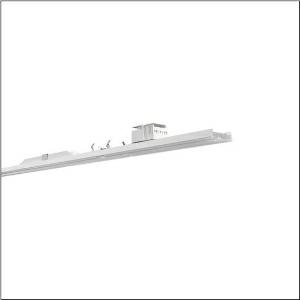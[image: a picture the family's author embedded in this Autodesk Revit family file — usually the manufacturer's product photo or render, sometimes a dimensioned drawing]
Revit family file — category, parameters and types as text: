
# Revit family: licross_r__11_recessed_mo_51tl11dv4fxf_3342
name_source: partatom
category: Lighting Fixtures
units: mm (PartAtom-declared; Revit-internal decimal feet)

## family parameters
Cut with Voids When Loaded = No
Host = Face
Light Source = No
Part Type = Normal
Room Calculation Point = No
Round Connector Dimension = Use Diameter
Shared = No

## types (1)
- --- (1 x LED, 15190 lm, 89.6 W, 4000K)
    Apparent Load = 90 VA
    CIE Flux Codes = 89 96 99 100 100
    Color Rendering = 80
    Color Temperature = 4000K
    Default Elevation = 1800 mm
    Description = Licross® 11 Recessed MOluminaire insert, length: 2.250mm, width: 66mm, height: 67mm, LED rated luminous flux: 15.190lm, light colour: 840, control gear: DALI 2, control gear: ECG DALI, with plug, 5-pole, with phase selection, mains connection: 220..240V, AC, 50/60Hz, halogen-free wiring, primary optical cover: cover, of PMMA, light emission: direct distribution, protection rating (complete): IP40, insulation class (complete): insulation class I (protective earthing), certification: CE, ENEC, VDE, protection symbol: D if used in an environment without relevant dust loads with corresponding accessories, permissible ambient temperature for indoor applications: -25..+35°C, corresponds to IFS (International Featured Standards) requirements for safety and quality in the food industry, reducing of maximum allowable ambient temperature of 5°C with ceiling mounting, packaging unit: 1 piece
    Height = 58 mm
    Lamp = 1 x LED
    Lamp Light Flux = 15190 lm
    Lamp Power = 89.6 W
    Lamp count = 1
    Length = 2250 mm
    Luminous efficacy = 170 lm/W
    Manufacturer = Siteco
    ModVariant = No
    Model = 51TL11DV4FXF
    Mounting Place = Ceiling
    Mounting Type = Pendant
    Number of Poles = 1
    OnlyDefault = Yes
    Power Factor = 1
    Product Name = Licross® 11 Recessed MO
    Product group = luminaire insert
    ProductGroupID = 902
    Protection Class = Protection class I
    Protection Degree = IP 40
    RLX_Detail_Level = 1
    RlxData = <blob elided: 27533 chars, md5=e8565715>
    Socket = socket
    Standby Power = 0 W
    System Light Flux = 15190 lm
    System Power = 90 W
    Type Comments = factory setting: luminous flux: 100 % | dim-lin: 254 | 400 mA
    Type Image = l_1266722.jpg
    URL = http://relux.com
    VarID = @adj_132994
    Voltage = 0 V
    Weight = 0.00 kg
    Width = 66 mm

## geometry (parser evidence)
native form markers: Blend x4, Sweep x9
no freeform markers — native parametric forms only
